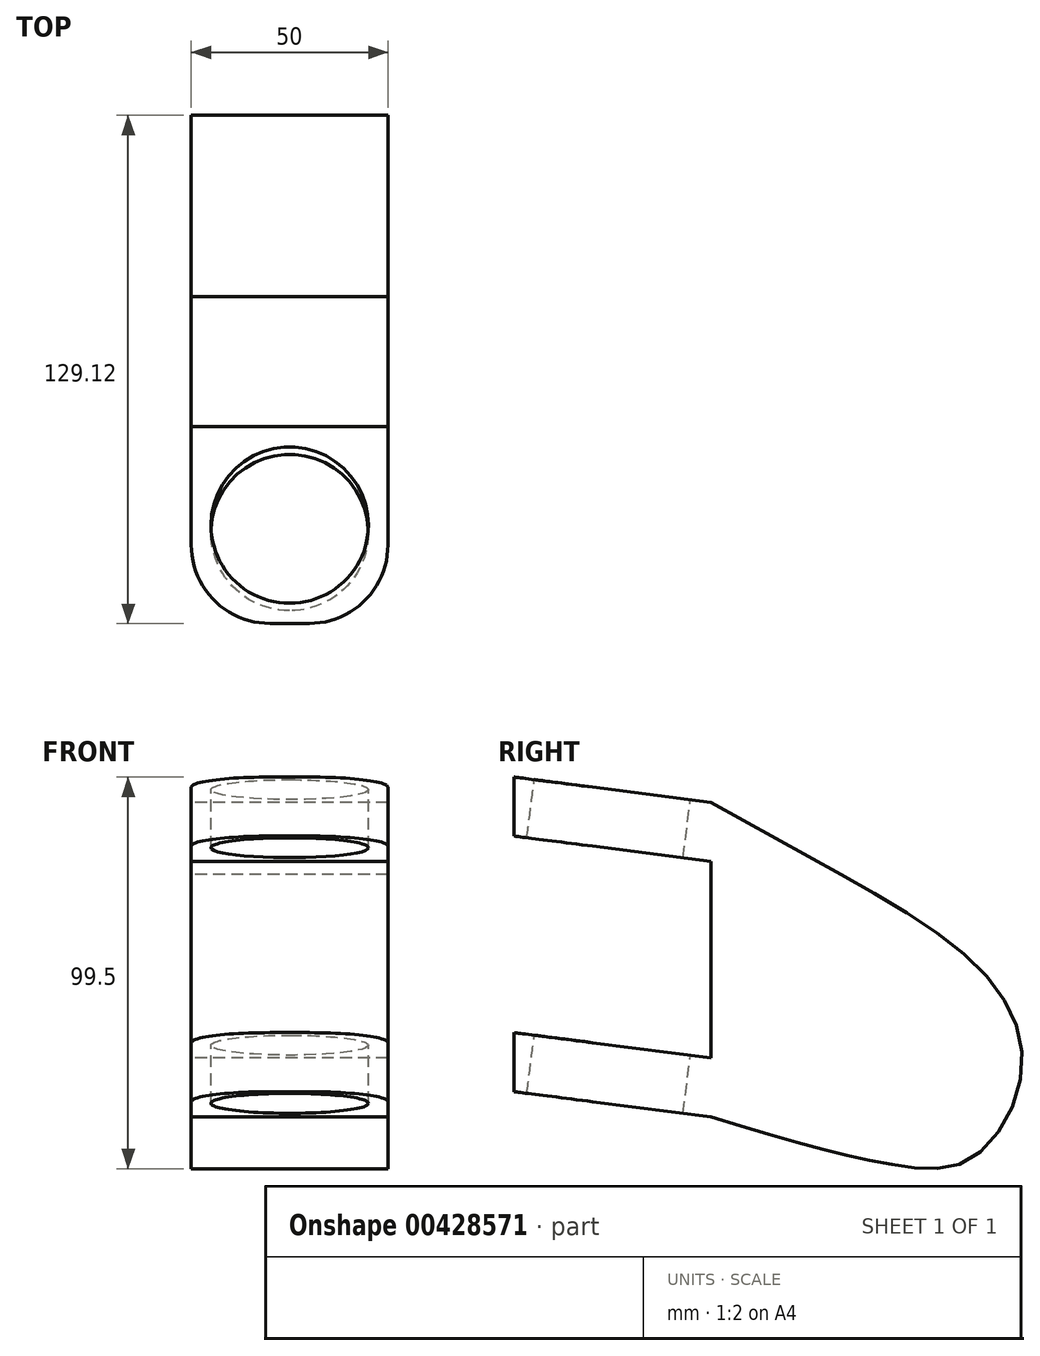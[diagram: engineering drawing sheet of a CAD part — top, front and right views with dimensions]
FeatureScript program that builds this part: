
annotation { "Feature Type Name" : "Feature", "Feature Type Description" : "" }
export const myFeature = defineFeature(function(context is Context, id is Id, definition is map)
    precondition{}
    {
        {
            var Q0;
            Q0=qCreatedBy(makeId("Right.planeOp"),FACE);
            var sketch = newSketch(context, id + "F0", { "sketchPlane" : qUnion([Q0])});
            skLineSegment(sketch, "E0", {"start": v(-47.86, 55.46) * mm, "end": v(-47.86, -24.47) * mm});
            skPoint(sketch, "E1", {"position": v(-47.86, -24.47) * mm});
            skPoint(sketch, "E2.orphan", {"position": v(-47.86, -29.87) * mm});
            skLineSegment(sketch, "E3", {"start": v(-47.86, 55.46) * mm, "end": v(-14.77, 37.16) * mm});
            skFitSpline(sketch, "E4", {"points": [v(-14.77, 37.16) * mm, v(22.16, 11.35) * mm, v(31.06, -13.34) * mm, v(17.92, -35.3) * mm, v(0, -36.85) * mm, v(-18.95, -32.87) * mm, v(-47.86, -24.47) * mm], "startDerivative": vector(196.12, -111.66) * mm, "endDerivative": vector(-172.48, 52.38) * mm});
            skLineSegment(sketch, "E5", {"start": v(-47.86, 55.46) * mm, "end": v(-97.86, 61.86) * mm});
            skLineSegment(sketch, "E6", {"start": v(-97.86, 61.86) * mm, "end": v(-97.86, 46.86) * mm});
            skLineSegment(sketch, "E7", {"start": v(-97.86, 46.86) * mm, "end": v(-47.86, 40.46) * mm});
            skLineSegment(sketch, "E8", {"start": v(-47.86, 40.46) * mm, "end": v(-47.86, -24.47) * mm});
            skLineSegment(sketch, "E9", {"start": v(-47.86, -24.47) * mm, "end": v(-97.86, -18.08) * mm});
            skLineSegment(sketch, "E10", {"start": v(-97.86, -18.08) * mm, "end": v(-97.86, -3.08) * mm});
            skLineSegment(sketch, "E11", {"start": v(-97.86, -3.08) * mm, "end": v(-47.86, -9.47) * mm});
            skSolve(sketch);
        }
        {
            var Q0;
            {var subQ0=sQuery(id+"F0.wireOp",EDGE,"E3");Q0=makeQuery(id+"F0.imprint","IMPRINT",FACE,{"disambiguationData":[TD([[makeQuery(id+"F0.imprint","IMPRINT",EDGE,{"derivedFrom":subQ0}),-1.0]])]});}
            var Q1;
            {var subQ2=sQuery(id+"F0.wireOp",EDGE,"E5");Q1=makeQuery(id+"F0.imprint","IMPRINT",FACE,{"disambiguationData":[TD([[makeQuery(id+"F0.imprint","IMPRINT",EDGE,{"derivedFrom":subQ2}),1.0]])]});}
            var Q2;
            {var subQ0=sQuery(id+"F0.wireOp",EDGE,"E9");Q2=makeQuery(id+"F0.imprint","IMPRINT",FACE,{"disambiguationData":[TD([[makeQuery(id+"F0.imprint","IMPRINT",EDGE,{"derivedFrom":subQ0}),-1.0]])]});}
            extrude(context, id + "F1", {"entities" : qUnion([Q0, Q1, Q2]), "depth" : 50 * mm});
        }
        {
            var Q0;
            Q0=makeQuery(id+"F1.opExtrude","SWEPT_FACE",FACE,{"disambiguationData":[OSD([sQuery(id+"F0.wireOp",EDGE,"E5")])]});
            var sketch = newSketch(context, id + "F2", { "sketchPlane" : qUnion([Q0])});
            skPoint(sketch, "E12", {"position": v(25, -79.71) * mm});
            skPoint(sketch, "E12.positionSnap0", {"position": v(25, -104.92) * mm});
            skPoint(sketch, "E12.positionSnap1", {"position": v(0, -79.71) * mm});
            skLineSegment(sketch, "E13.bottom", {"start": v(0, -54.5) * mm, "end": v(50, -54.5) * mm});
            skLineSegment(sketch, "E13.top", {"start": v(0, -104.92) * mm, "end": v(50, -104.92) * mm});
            skLineSegment(sketch, "E13.left", {"start": v(0, -54.5) * mm, "end": v(0, -104.92) * mm});
            skLineSegment(sketch, "E13.right", {"start": v(50, -54.5) * mm, "end": v(50, -104.92) * mm});
            skCircle(sketch, "E14", {"center": v(25, -79.71) * mm, "radius": 25 * mm});
            skCircle(sketch, "E15.0", {"center": v(25, -79.71) * mm, "radius": 20 * mm});
            skSolve(sketch);
        }
        {
            var Q0;
            Q0=makeQuery(id+"F1.opExtrude","SWEPT_FACE",FACE,{"disambiguationData":[OSD([sQuery(id+"F0.wireOp",EDGE,"E11")])]});
            var sketch = newSketch(context, id + "F3", { "sketchPlane" : qUnion([Q0])});
            skPoint(sketch, "E16", {"position": v(25, -71.47) * mm});
            skPoint(sketch, "E16.positionSnap0", {"position": v(0, -71.47) * mm});
            skPoint(sketch, "E16.positionSnap1", {"position": v(25, -46.27) * mm});
            skLineSegment(sketch, "E17.bottom", {"start": v(0, -46.27) * mm, "end": v(50, -46.27) * mm});
            skLineSegment(sketch, "E17.top", {"start": v(0, -96.68) * mm, "end": v(50, -96.68) * mm});
            skLineSegment(sketch, "E17.left", {"start": v(0, -46.27) * mm, "end": v(0, -96.68) * mm});
            skLineSegment(sketch, "E17.right", {"start": v(50, -46.27) * mm, "end": v(50, -96.68) * mm});
            skCircle(sketch, "E18", {"center": v(25, -71.47) * mm, "radius": 25 * mm});
            skCircle(sketch, "E19.0", {"center": v(25, -71.47) * mm, "radius": 20 * mm});
            skSolve(sketch);
        }
        {
            var Q0;
            Q0=makeQuery(id+"F2.imprint","IMPRINT",FACE,{"disambiguationData":[TD([[makeQuery(id+"F2.imprint","IMPRINT",EDGE,{"derivedFrom":sQuery(id+"F2.wireOp",EDGE,"E15.0")}),1.0]])]});
            var Q1;
            Q1=makeQuery(id+"F3.imprint","IMPRINT",FACE,{"disambiguationData":[TD([[makeQuery(id+"F3.imprint","IMPRINT",EDGE,{"derivedFrom":sQuery(id+"F3.wireOp",EDGE,"E19.0")}),1.0]])]});
            extrude(context, id + "F4", {"entities" : qUnion([Q0, Q1]), "operationType" : NewBodyOperationType.REMOVE, "oppositeDirection" : true, "depth" : 25 * mm});
        }
        {
            var Q0;
            Q0=makeQuery(id+"F1.opExtrude","CAP_EDGE",EDGE,{"disambiguationData":[OSD([sQuery(id+"F0.wireOp",EDGE,"E6")])],"isStart":true});
            var Q1;
            Q1=makeQuery(id+"F1.opExtrude","CAP_EDGE",EDGE,{"disambiguationData":[OSD([sQuery(id+"F0.wireOp",EDGE,"E6")])],"isStart":false});
            var Q2;
            Q2=makeQuery(id+"F1.opExtrude","CAP_EDGE",EDGE,{"disambiguationData":[OSD([sQuery(id+"F0.wireOp",EDGE,"E10")])],"isStart":true});
            var Q3;
            Q3=makeQuery(id+"F1.opExtrude","CAP_EDGE",EDGE,{"disambiguationData":[OSD([sQuery(id+"F0.wireOp",EDGE,"E10")])],"isStart":false});
            fillet(context, id + "F5", {"entities" : qUnion([Q0, Q1, Q2, Q3]), "radius" : 20 * mm, "tangentPropagation" : true, "allowEdgeOverflow" : false});
        }
    });
